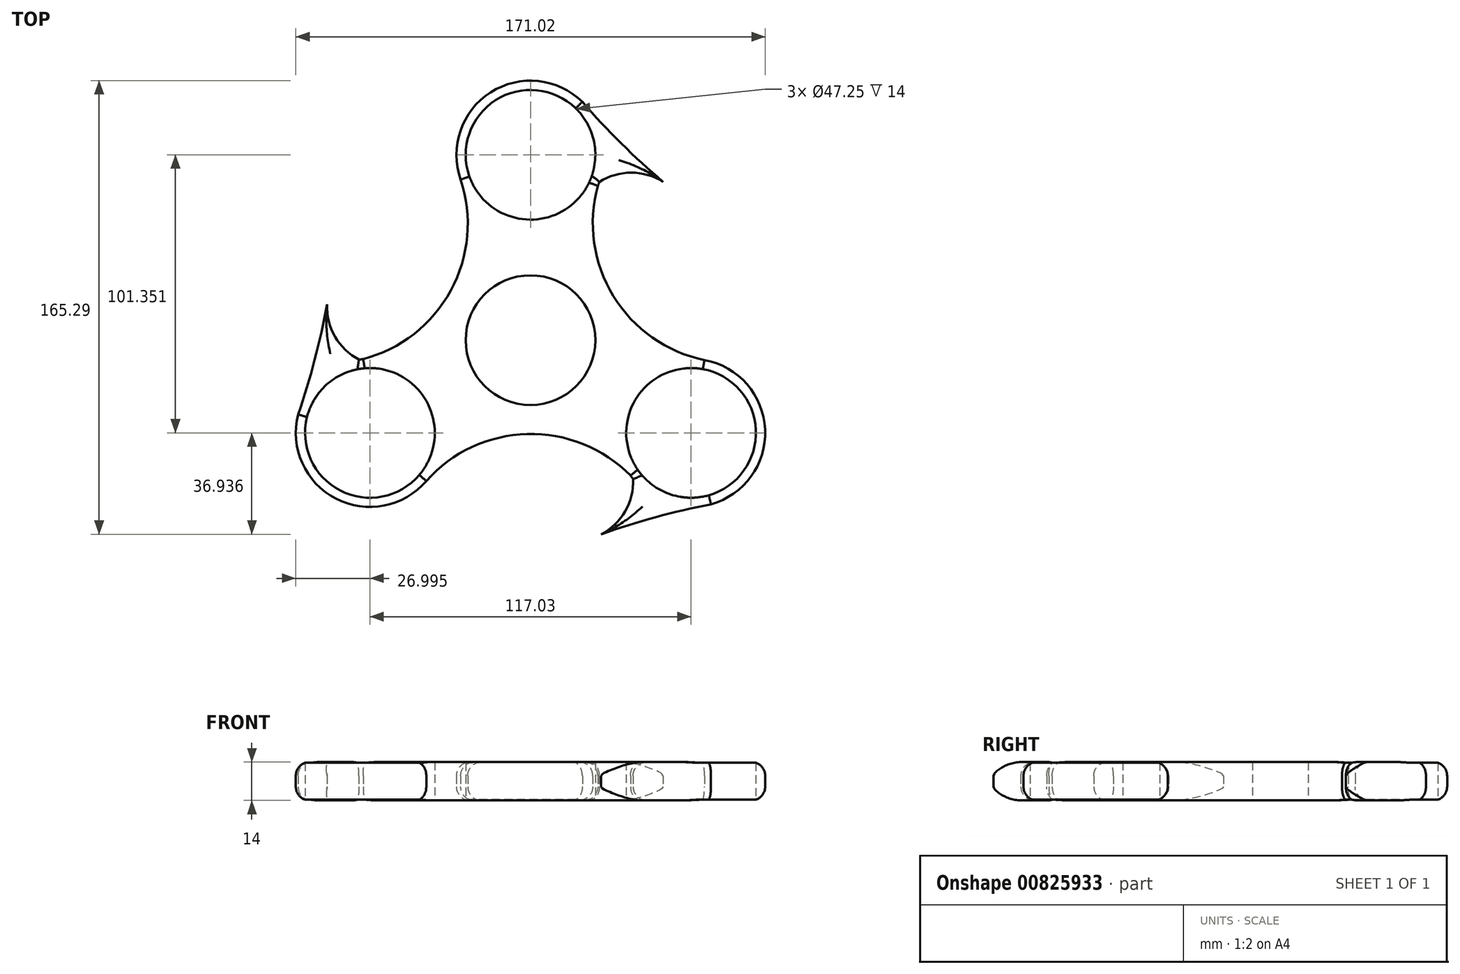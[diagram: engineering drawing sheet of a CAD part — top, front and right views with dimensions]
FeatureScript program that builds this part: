
annotation { "Feature Type Name" : "Feature", "Feature Type Description" : "" }
export const myFeature = defineFeature(function(context is Context, id is Id, definition is map)
    precondition{}
    {
        {
            var Q0;
            Q0=qCreatedBy(makeId("Top.planeOp"),FACE);
            var sketch = newSketch(context, id + "F0", { "sketchPlane" : qUnion([Q0])});
            skCircle(sketch, "E0", {"center": v(0, 0) * mm, "radius": 23.62 * mm});
            skCircle(sketch, "E1", {"center": v(0, 67.57) * mm, "radius": 23.62 * mm});
            skArc(sketch, "E2", {"start": v(24.51, 56.25) * mm, "mid": v(24.83, 56.96) * mm, "end": v(25.12, 57.67) * mm});
            skCircle(sketch, "E3.1.0", {"center": v(-58.51, -33.78) * mm, "radius": 23.62 * mm});
            skArc(sketch, "E3.1.1", {"start": v(-60.97, -6.9) * mm, "mid": v(-61.74, -6.98) * mm, "end": v(-62.5, -7.08) * mm});
            skCircle(sketch, "E3.2.0", {"center": v(58.51, -33.78) * mm, "radius": 23.62 * mm});
            skArc(sketch, "E3.2.1", {"start": v(36.46, -49.36) * mm, "mid": v(36.91, -49.98) * mm, "end": v(37.38, -50.6) * mm});
            skArc(sketch, "E4.1.0", {"start": v(-60.97, -6.9) * mm, "mid": v(-29.03, 18.12) * mm, "end": v(-25.44, 58.53) * mm});
            skPoint(sketch, "E5.orphan", {"position": v(63.41, -7.23) * mm});
            skPoint(sketch, "E6.orphan", {"position": v(-37.97, -51.3) * mm});
            skArc(sketch, "E7.1.0", {"start": v(36.46, -49.36) * mm, "mid": v(-1.18, -34.2) * mm, "end": v(-37.97, -51.3) * mm});
            skArc(sketch, "E7.2.0", {"start": v(24.51, 56.25) * mm, "mid": v(30.2, 16.08) * mm, "end": v(63.41, -7.23) * mm});
            skArc(sketch, "E8", {"start": v(18.9, 86.84) * mm, "mid": v(33.1, 71.7) * mm, "end": v(48.37, 57.67) * mm});
            skArc(sketch, "E9", {"start": v(48.37, 57.67) * mm, "mid": v(36.75, 61.06) * mm, "end": v(25.12, 57.67) * mm});
            skArc(sketch, "E10.1.0", {"start": v(-84.66, -27.05) * mm, "mid": v(-78.65, -7.2) * mm, "end": v(-74.13, 13.05) * mm});
            skArc(sketch, "E10.1.1", {"start": v(-74.13, 13.05) * mm, "mid": v(-71.25, 1.3) * mm, "end": v(-62.5, -7.08) * mm});
            skArc(sketch, "E10.2.0", {"start": v(65.75, -59.8) * mm, "mid": v(45.55, -64.51) * mm, "end": v(25.76, -70.72) * mm});
            skArc(sketch, "E10.2.1", {"start": v(25.76, -70.72) * mm, "mid": v(34.5, -62.35) * mm, "end": v(37.38, -50.6) * mm});
            skArc(sketch, "E11.trimOffspring", {"start": v(-83.42, -23.35) * mm, "mid": v(-72.66, -56.78) * mm, "end": v(-37.97, -51.3) * mm});
            skPoint(sketch, "E12.orphan", {"position": v(-66.65, -8.04) * mm});
            skArc(sketch, "E13.trimOffspring", {"start": v(21.48, 83.92) * mm, "mid": v(-12.85, 91.31) * mm, "end": v(-25.44, 58.53) * mm});
            skPoint(sketch, "E14.orphan", {"position": v(26.36, 61.74) * mm});
            skArc(sketch, "E15.trimOffspring", {"start": v(61.93, -60.57) * mm, "mid": v(85.5, -34.53) * mm, "end": v(63.41, -7.23) * mm});
            skPoint(sketch, "E16.orphan", {"position": v(40.29, -53.7) * mm});
            skSolve(sketch);
        }
        {
            var Q0;
            Q0=makeQuery(id+"F0.imprint","IMPRINT",FACE,{"disambiguationData":[TD([[makeQuery(id+"F0.imprint","IMPRINT",EDGE,{"derivedFrom":sQuery(id+"F0.wireOp",EDGE,"E0")}),-1.0]])]});
            extrude(context, id + "F1", {"entities" : qUnion([Q0]), "depth" : 14 * mm, "offsetDistance" : 25 * mm});
        }
        {
            var Q0;
            Q0=makeQuery(id+"F1.opExtrude","CAP_EDGE",EDGE,{"disambiguationData":[OSD([sQuery(id+"F0.wireOp",EDGE,"E7.1.0")])],"isStart":false});
            var Q1;
            Q1=makeQuery(id+"F1.opExtrude","CAP_EDGE",EDGE,{"disambiguationData":[OSD([sQuery(id+"F0.wireOp",EDGE,"E11.trimOffspring")])],"isStart":false});
            var Q2;
            Q2=makeQuery(id+"F1.opExtrude","CAP_EDGE",EDGE,{"disambiguationData":[OSD([sQuery(id+"F0.wireOp",EDGE,"E10.1.0")])],"isStart":false});
            var Q3;
            Q3=makeQuery(id+"F1.opExtrude","CAP_EDGE",EDGE,{"disambiguationData":[OSD([sQuery(id+"F0.wireOp",EDGE,"E10.1.1")])],"isStart":false});
            var Q4;
            Q4=makeQuery(id+"F1.opExtrude","CAP_EDGE",EDGE,{"disambiguationData":[OSD([sQuery(id+"F0.wireOp",EDGE,"E4.1.0")])],"isStart":false});
            var Q5;
            Q5=makeQuery(id+"F1.opExtrude","CAP_EDGE",EDGE,{"disambiguationData":[OSD([sQuery(id+"F0.wireOp",EDGE,"E13.trimOffspring")])],"isStart":false});
            var Q6;
            Q6=makeQuery(id+"F1.opExtrude","CAP_EDGE",EDGE,{"disambiguationData":[OSD([sQuery(id+"F0.wireOp",EDGE,"E8")])],"isStart":false});
            var Q7;
            Q7=makeQuery(id+"F1.opExtrude","CAP_EDGE",EDGE,{"disambiguationData":[OSD([sQuery(id+"F0.wireOp",EDGE,"E9")])],"isStart":false});
            var Q8;
            Q8=makeQuery(id+"F1.opExtrude","CAP_EDGE",EDGE,{"disambiguationData":[OSD([sQuery(id+"F0.wireOp",EDGE,"E7.2.0")])],"isStart":false});
            var Q9;
            Q9=makeQuery(id+"F1.opExtrude","CAP_EDGE",EDGE,{"disambiguationData":[OSD([sQuery(id+"F0.wireOp",EDGE,"E10.2.1")])],"isStart":false});
            var Q10;
            Q10=makeQuery(id+"F1.opExtrude","CAP_EDGE",EDGE,{"disambiguationData":[OSD([sQuery(id+"F0.wireOp",EDGE,"E10.2.0")])],"isStart":false});
            var Q11;
            Q11=makeQuery(id+"F1.opExtrude","CAP_EDGE",EDGE,{"disambiguationData":[OSD([sQuery(id+"F0.wireOp",EDGE,"E15.trimOffspring")])],"isStart":false});
            var Q12;
            Q12=makeQuery(id+"F1.opExtrude","CAP_EDGE",EDGE,{"disambiguationData":[OSD([sQuery(id+"F0.wireOp",EDGE,"E7.2.0")])],"isStart":true});
            var Q13;
            Q13=makeQuery(id+"F1.opExtrude","CAP_EDGE",EDGE,{"disambiguationData":[OSD([sQuery(id+"F0.wireOp",EDGE,"E15.trimOffspring")])],"isStart":true});
            var Q14;
            Q14=makeQuery(id+"F1.opExtrude","CAP_EDGE",EDGE,{"disambiguationData":[OSD([sQuery(id+"F0.wireOp",EDGE,"E10.2.1")])],"isStart":true});
            var Q15;
            Q15=makeQuery(id+"F1.opExtrude","CAP_EDGE",EDGE,{"disambiguationData":[OSD([sQuery(id+"F0.wireOp",EDGE,"E10.2.0")])],"isStart":true});
            var Q16;
            Q16=makeQuery(id+"F1.opExtrude","CAP_EDGE",EDGE,{"disambiguationData":[OSD([sQuery(id+"F0.wireOp",EDGE,"E7.1.0")])],"isStart":true});
            var Q17;
            Q17=makeQuery(id+"F1.opExtrude","CAP_EDGE",EDGE,{"disambiguationData":[OSD([sQuery(id+"F0.wireOp",EDGE,"E11.trimOffspring")])],"isStart":true});
            var Q18;
            Q18=makeQuery(id+"F1.opExtrude","CAP_EDGE",EDGE,{"disambiguationData":[OSD([sQuery(id+"F0.wireOp",EDGE,"E10.1.0")])],"isStart":true});
            var Q19;
            Q19=makeQuery(id+"F1.opExtrude","CAP_EDGE",EDGE,{"disambiguationData":[OSD([sQuery(id+"F0.wireOp",EDGE,"E4.1.0")])],"isStart":true});
            var Q20;
            Q20=makeQuery(id+"F1.opExtrude","CAP_EDGE",EDGE,{"disambiguationData":[OSD([sQuery(id+"F0.wireOp",EDGE,"E10.1.1")])],"isStart":true});
            var Q21;
            Q21=makeQuery(id+"F1.opExtrude","CAP_EDGE",EDGE,{"disambiguationData":[OSD([sQuery(id+"F0.wireOp",EDGE,"E13.trimOffspring")])],"isStart":true});
            var Q22;
            Q22=makeQuery(id+"F1.opExtrude","CAP_EDGE",EDGE,{"disambiguationData":[OSD([sQuery(id+"F0.wireOp",EDGE,"E8")])],"isStart":true});
            var Q23;
            Q23=makeQuery(id+"F1.opExtrude","CAP_EDGE",EDGE,{"disambiguationData":[OSD([sQuery(id+"F0.wireOp",EDGE,"E9")])],"isStart":true});
            fillet(context, id + "F2", {"entities" : qUnion([Q0, Q1, Q2, Q3, Q4, Q5, Q6, Q7, Q8, Q9, Q10, Q11, Q12, Q13, Q14, Q15, Q16, Q17, Q18, Q19, Q20, Q21, Q22, Q23]), "radius" : 5 * mm, "tangentPropagation" : true, "allowEdgeOverflow" : false});
        }
        {
            var Q0;
            Q0=makeQuery(id+"F1.opExtrude","CAP_EDGE",EDGE,{"disambiguationData":[OSD([sQuery(id+"F0.wireOp",EDGE,"E3.1.1")])],"isStart":false});
            var Q1;
            Q1=makeQuery(id+"F1.opExtrude","CAP_EDGE",EDGE,{"disambiguationData":[OSD([sQuery(id+"F0.wireOp",EDGE,"E3.1.1")])],"isStart":true});
            var Q2;
            Q2=makeQuery(id+"F1.opExtrude","CAP_EDGE",EDGE,{"disambiguationData":[OSD([sQuery(id+"F0.wireOp",EDGE,"E2")])],"isStart":false});
            var Q3;
            Q3=makeQuery(id+"F1.opExtrude","CAP_EDGE",EDGE,{"disambiguationData":[OSD([sQuery(id+"F0.wireOp",EDGE,"E2")])],"isStart":true});
            var Q4;
            Q4=makeQuery(id+"F1.opExtrude","CAP_EDGE",EDGE,{"disambiguationData":[OSD([sQuery(id+"F0.wireOp",EDGE,"E3.2.1")])],"isStart":false});
            var Q5;
            Q5=makeQuery(id+"F1.opExtrude","CAP_EDGE",EDGE,{"disambiguationData":[OSD([sQuery(id+"F0.wireOp",EDGE,"E3.2.1")])],"isStart":true});
            fillet(context, id + "F3", {"entities" : qUnion([Q0, Q1, Q2, Q3, Q4, Q5]), "radius" : 5 * mm, "tangentPropagation" : true, "allowEdgeOverflow" : false});
        }
    });
